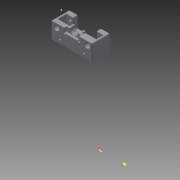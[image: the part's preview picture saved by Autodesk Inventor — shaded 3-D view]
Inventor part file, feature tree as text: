
AUTODESK INVENTOR PART (.ipt)
format: ipt  version: 2014 (Build 180170000, 170)  size: 352,256 bytes
history: native  units: in
note: dims shown in document units (in); Inventor stores cm internally (conversion verified against a paired STEP export)
features: reference x14, sketch x11, extrude x10, plane x3, fillet x1, move_body x1
ambient origin geometry x8: Origin, YZ Plane, XZ Plane, XY Plane, X Axis, Y Axis, Z Axis, Center Point
bodies: Solid1 (feature_tree)
feature tree (40):
  plane  "Work Plane1"
  extrude  "Extrusion1"  Depth=0.1in
  extrude  "Extrusion2"  Depth=0.4528in TaperAngle=0.0deg
  extrude  "Extrusion3"  Depth=0.4724in
  extrude  "Extrusion4"  Depth=0.4724in
  sketch  "Sketch5"  dims[d14=0.1181in d15=0.1181in]
  extrude  "Extrusion5"  Depth=0.1181in
  extrude  "Extrusion6"  Depth=0.6024in TaperAngle=0.0deg
  sketch  "Sketch8"  dims[d22=0.1969in d23=0.1181in d24=0.1181in]
  plane  "Work Plane2"
  extrude  "Extrusion7"  Depth=0.1181in
  sketch  "Sketch9"  dims[d25=6.0in d26=0.0in d28=0.1004in d29=0.0in]
  plane  "Work Plane3"
  extrude  "Extrusion8"  Depth=0.1181in
  fillet  "Fillet2"  Radius=0.1181in
  extrude  "Extrusion9"  Depth=0.1004in TaperAngle=0.0deg
  extrude  "Extrusion10"  Depth=0.2165in
  move_body  "Move Body1"
  sketch  "Sketch1"  dims[d2=0.1969in d3=0.0in d4=0.1in]
  reference  "Reference1"
  reference  "Reference2"
  reference  "Reference3"
  reference  "Reference4"
  reference  "Reference5"
  reference  "Reference6"
  reference  "Reference7"
  reference  "Reference8"
  reference  "Reference9"
  reference  "Reference10"
  reference  "Reference11"
  sketch  "Sketch2"  dims[d5=0.1in d6=0.4528in d7=0.0in]
  sketch  "Sketch3"  dims[d10=0.6102in d11=0.4724in]
  reference  "Reference12"
  reference  "Reference13"
  sketch  "Sketch4"  dims[d12=0.6102in d13=0.4724in]
  sketch  "Sketch6"  dims[d16=0.2087in d17=0.0in d18=0.6024in d19=0.0in]
  sketch  "Sketch7"  dims[d20=0.1181in d21=0.1181in]
  reference  "Reference14"
  sketch  "Sketch10"  dims[d30=0.0988in d31=0.0in d32=0.2165in]
  sketch  "Sketch11"  dims[d33=0.2953in d34=0.0988in d35=0.0in d36=0.0394in d37=0.0787in d38=0.0787in d39=0.0787in d40=0.0787in d41=0.0787in d42=0.1969in d43=0.0in d44=0.2756in d45=0.2756in d46=0.1969in d47=0.0in d48=-1.4in d49=4.3in d50=0.0in]
